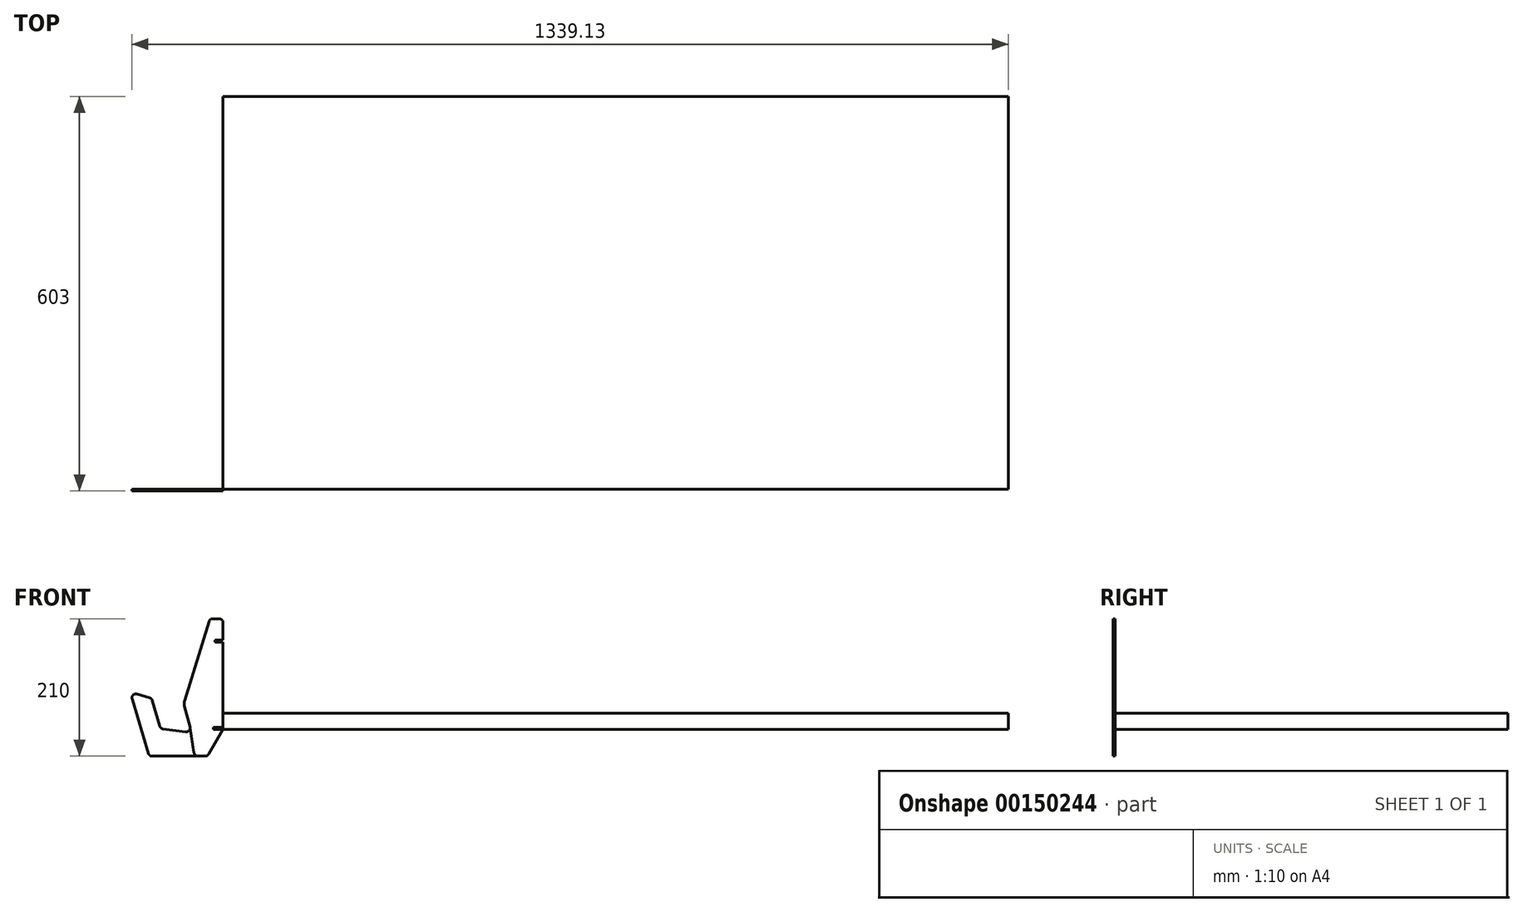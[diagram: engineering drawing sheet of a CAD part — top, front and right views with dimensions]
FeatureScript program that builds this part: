
annotation { "Feature Type Name" : "Feature", "Feature Type Description" : "" }
export const myFeature = defineFeature(function(context is Context, id is Id, definition is map)
    precondition{}
    {
        {
            var Q0;
            Q0=qCreatedBy(makeId("Front.planeOp"),FACE);
            var sketch = newSketch(context, id + "F0", { "sketchPlane" : qUnion([Q0])});
            skLineSegment(sketch, "E0", {"start": v(0, 163.1) * mm, "end": v(0, 136.2) * mm});
            skLineSegment(sketch, "E1", {"start": v(0, 0) * mm, "end": v(-21.82, -37.8) * mm});
            skLineSegment(sketch, "E2", {"start": v(-27.08, -40.83) * mm, "end": v(-38.38, -40.83) * mm});
            skLineSegment(sketch, "E3", {"start": v(-50.57, 3.79) * mm, "end": v(-51.22, 6.26) * mm});
            skLineSegment(sketch, "E4", {"start": v(-58.74, 44.08) * mm, "end": v(-21.32, 164.9) * mm});
            skLineSegment(sketch, "E5", {"start": v(-15.52, 169.17) * mm, "end": v(-6.07, 169.17) * mm});
            skLineSegment(sketch, "E6.bottom", {"start": v(0, 0.2) * mm, "end": v(-15, 0.2) * mm});
            skLineSegment(sketch, "E6.top", {"start": v(0, 3.2) * mm, "end": v(-15, 3.2) * mm});
            skLineSegment(sketch, "E6.right", {"start": v(-15, 0.2) * mm, "end": v(-15, 3.2) * mm});
            skLineSegment(sketch, "E7.trimOffspring", {"start": v(0, 0.2) * mm, "end": v(0, 0) * mm});
            skLineSegment(sketch, "E8.bottom", {"start": v(0, 136.2) * mm, "end": v(-12, 136.2) * mm});
            skLineSegment(sketch, "E8.top", {"start": v(0, 133.2) * mm, "end": v(-12, 133.2) * mm});
            skLineSegment(sketch, "E8.right", {"start": v(-12, 136.2) * mm, "end": v(-12, 133.2) * mm});
            skLineSegment(sketch, "E9.trimOffspring", {"start": v(0, 133.2) * mm, "end": v(0, 3.2) * mm});
            skLineSegment(sketch, "E10", {"start": v(-113.63, -37.4) * mm, "end": v(-138.87, 46.45) * mm});
            skLineSegment(sketch, "E11", {"start": v(-131.3, 54) * mm, "end": v(-111.93, 48.1) * mm});
            skLineSegment(sketch, "E12", {"start": v(-107.87, 43.99) * mm, "end": v(-96.47, 4.82) * mm});
            skLineSegment(sketch, "E13", {"start": v(-91.4, 0.49) * mm, "end": v(-57.2, -3.77) * mm});
            skPoint(sketch, "E14.visualSharp", {"position": v(-142.14, 57.3) * mm});
            skArc(sketch, "E14.filletArc", {"start": v(-131.3, 54) * mm, "mid": v(-137.35, 52.5) * mm, "end": v(-138.87, 46.45) * mm});
            skPoint(sketch, "E15.visualSharp", {"position": v(-108.78, 47.14) * mm});
            skArc(sketch, "E15.filletArc", {"start": v(-107.87, 43.99) * mm, "mid": v(-109.38, 46.56) * mm, "end": v(-111.93, 48.1) * mm});
            skPoint(sketch, "E16.visualSharp", {"position": v(-95.35, 0.98) * mm});
            skArc(sketch, "E16.filletArc", {"start": v(-96.47, 4.82) * mm, "mid": v(-94.58, 1.9) * mm, "end": v(-91.4, 0.49) * mm});
            skLineSegment(sketch, "E17", {"start": v(-51.22, 6.26) * mm, "end": v(-58.92, 35.86) * mm});
            skArc(sketch, "E18.filletArc", {"start": v(-57.2, -3.77) * mm, "mid": v(-51.88, -1.75) * mm, "end": v(-50.57, 3.79) * mm});
            skLineSegment(sketch, "E19", {"start": v(-50.57, 3.79) * mm, "end": v(-44.38, -35.7) * mm});
            skPoint(sketch, "E20.visualSharp", {"position": v(-114.76, -33.65) * mm});
            skArc(sketch, "E20.filletArc", {"start": v(-113.63, -37.4) * mm, "mid": v(-112.34, -39.54) * mm, "end": v(-110.19, -40.78) * mm});
            skPoint(sketch, "E21.visualSharp", {"position": v(-60, 40) * mm});
            skArc(sketch, "E21.filletArc", {"start": v(-58.74, 44.08) * mm, "mid": v(-59.4, 39.99) * mm, "end": v(-58.92, 35.86) * mm});
            skPoint(sketch, "E22.visualSharp", {"position": v(-20, 169.17) * mm});
            skArc(sketch, "E22.filletArc", {"start": v(-15.52, 169.17) * mm, "mid": v(-19.13, 167.98) * mm, "end": v(-21.32, 164.9) * mm});
            skPoint(sketch, "E23.visualSharp", {"position": v(0, 169.17) * mm});
            skArc(sketch, "E23.filletArc", {"start": v(0, 163.1) * mm, "mid": v(-1.78, 167.4) * mm, "end": v(-6.07, 169.17) * mm});
            skPoint(sketch, "E24.visualSharp", {"position": v(-23.57, -40.83) * mm});
            skArc(sketch, "E24.filletArc", {"start": v(-27.08, -40.83) * mm, "mid": v(-24.04, -40.02) * mm, "end": v(-21.82, -37.8) * mm});
            skPoint(sketch, "E25.visualSharp", {"position": v(-43.57, -40.83) * mm});
            skArc(sketch, "E25.filletArc", {"start": v(-44.38, -35.7) * mm, "mid": v(-42.33, -39.37) * mm, "end": v(-38.38, -40.83) * mm});
            skLineSegment(sketch, "E26", {"start": v(-110.19, -40.78) * mm, "end": v(-38.38, -40.83) * mm});
            skSolve(sketch);
        }
        {
            var Q0;
            Q0=makeQuery(id+"F0.imprint","IMPRINT",FACE,{"disambiguationData":[TD([[makeQuery(id+"F0.imprint","IMPRINT",EDGE,{"derivedFrom":sQuery(id+"F0.wireOp",EDGE,"E0")}),-1.0]])]});
            extrude(context, id + "F1", {"entities" : qUnion([Q0]), "depth" : 3 * mm});
        }
        {
            var Q0;
            Q0=qCreatedBy(makeId("Top.planeOp"),FACE);
            var sketch = newSketch(context, id + "F2", { "sketchPlane" : qUnion([Q0])});
            skLineSegment(sketch, "E27.bottom", {"start": v(0, 600) * mm, "end": v(1200, 600) * mm});
            skLineSegment(sketch, "E27.top", {"start": v(0, 0) * mm, "end": v(1200, 0) * mm});
            skLineSegment(sketch, "E27.left", {"start": v(0, 600) * mm, "end": v(0, 0) * mm});
            skLineSegment(sketch, "E27.right", {"start": v(1200, 600) * mm, "end": v(1200, 0) * mm});
            skSolve(sketch);
        }
        {
            var Q0;
            Q0 = qSketchRegion(id + "F2", true);
            extrude(context, id + "F3", {"entities" : qUnion([Q0]), "depth" : 25 * mm});
        }
        {
            var Q0;
            Q0=makeQuery(id+"F0.imprint","IMPRINT",FACE,{"disambiguationData":[TD([[makeQuery(id+"F0.imprint","IMPRINT",EDGE,{"derivedFrom":sQuery(id+"F0.wireOp",EDGE,"E10")}),-1.0]])]});
            var Q1;
            Q1=makeQuery(id+"F0.imprint","IMPRINT",FACE,{"disambiguationData":[TD([[makeQuery(id+"F0.imprint","IMPRINT",EDGE,{"derivedFrom":sQuery(id+"F0.wireOp",EDGE,"E0")}),-1.0]])]});
            extrude(context, id + "F4", {"entities" : qUnion([Q0, Q1]), "depth" : 3 * mm});
        }
    });
